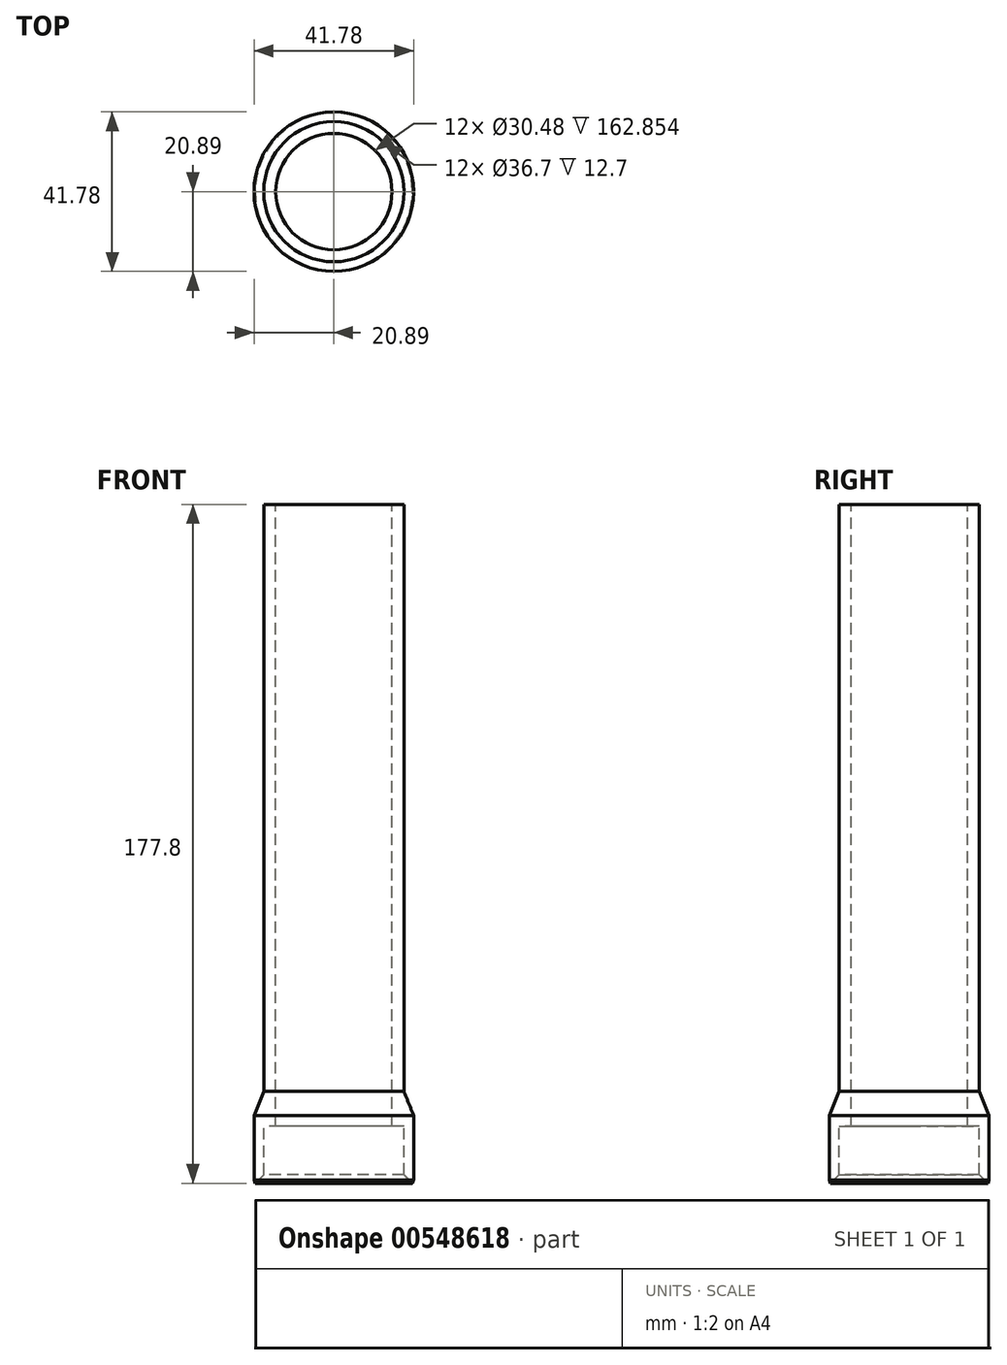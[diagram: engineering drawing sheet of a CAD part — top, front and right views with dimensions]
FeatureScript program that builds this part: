
annotation { "Feature Type Name" : "Feature", "Feature Type Description" : "" }
export const myFeature = defineFeature(function(context is Context, id is Id, definition is map)
    precondition{}
    {
        {
            var Q0;
            Q0=qCreatedBy(makeId("Front.planeOp"),FACE);
            var sketch = newSketch(context, id + "F0", { "sketchPlane" : qUnion([Q0])});
            skLineSegment(sketch, "E0", {"start": v(15.24, 90.33) * mm, "end": v(18.35, 90.33) * mm});
            skLineSegment(sketch, "E1", {"start": v(18.35, 90.33) * mm, "end": v(18.35, -63.38) * mm});
            skLineSegment(sketch, "E2", {"start": v(18.35, -63.38) * mm, "end": v(20.9, -69.7) * mm});
            skLineSegment(sketch, "E3", {"start": v(20.9, -69.7) * mm, "end": v(20.9, -86.64) * mm});
            skLineSegment(sketch, "E4", {"start": v(20.9, -86.64) * mm, "end": v(20.6, -87.47) * mm});
            skLineSegment(sketch, "E5", {"start": v(20.6, -87.47) * mm, "end": v(18.35, -85.22) * mm});
            skLineSegment(sketch, "E6", {"start": v(18.35, -85.22) * mm, "end": v(18.35, -72.52) * mm});
            skLineSegment(sketch, "E7", {"start": v(18.35, -72.52) * mm, "end": v(15.24, -72.52) * mm});
            skLineSegment(sketch, "E8", {"start": v(15.24, -72.52) * mm, "end": v(15.24, 90.33) * mm});
            skSolve(sketch);
        }
        {
            var Q0;
            Q0=qCreatedBy(makeId("Front.planeOp"),FACE);
            var sketch = newSketch(context, id + "F1", { "sketchPlane" : qUnion([Q0])});
            skLineSegment(sketch, "E9", {"start": v(0, 76.3) * mm, "end": v(0, -76.12) * mm});
            skSolve(sketch);
        }
        {
            var Q0;
            Q0 = qSketchRegion(id + "F0", true);
            var Q1;
            Q1=sQuery(id+"F1.wireOp",EDGE,"E9");
            revolve(context, id + "F2", {"entities" : qUnion([Q0]), "axis" : qUnion([Q1]), "revolveType" : RevolveType.FULL});
        }
    });
